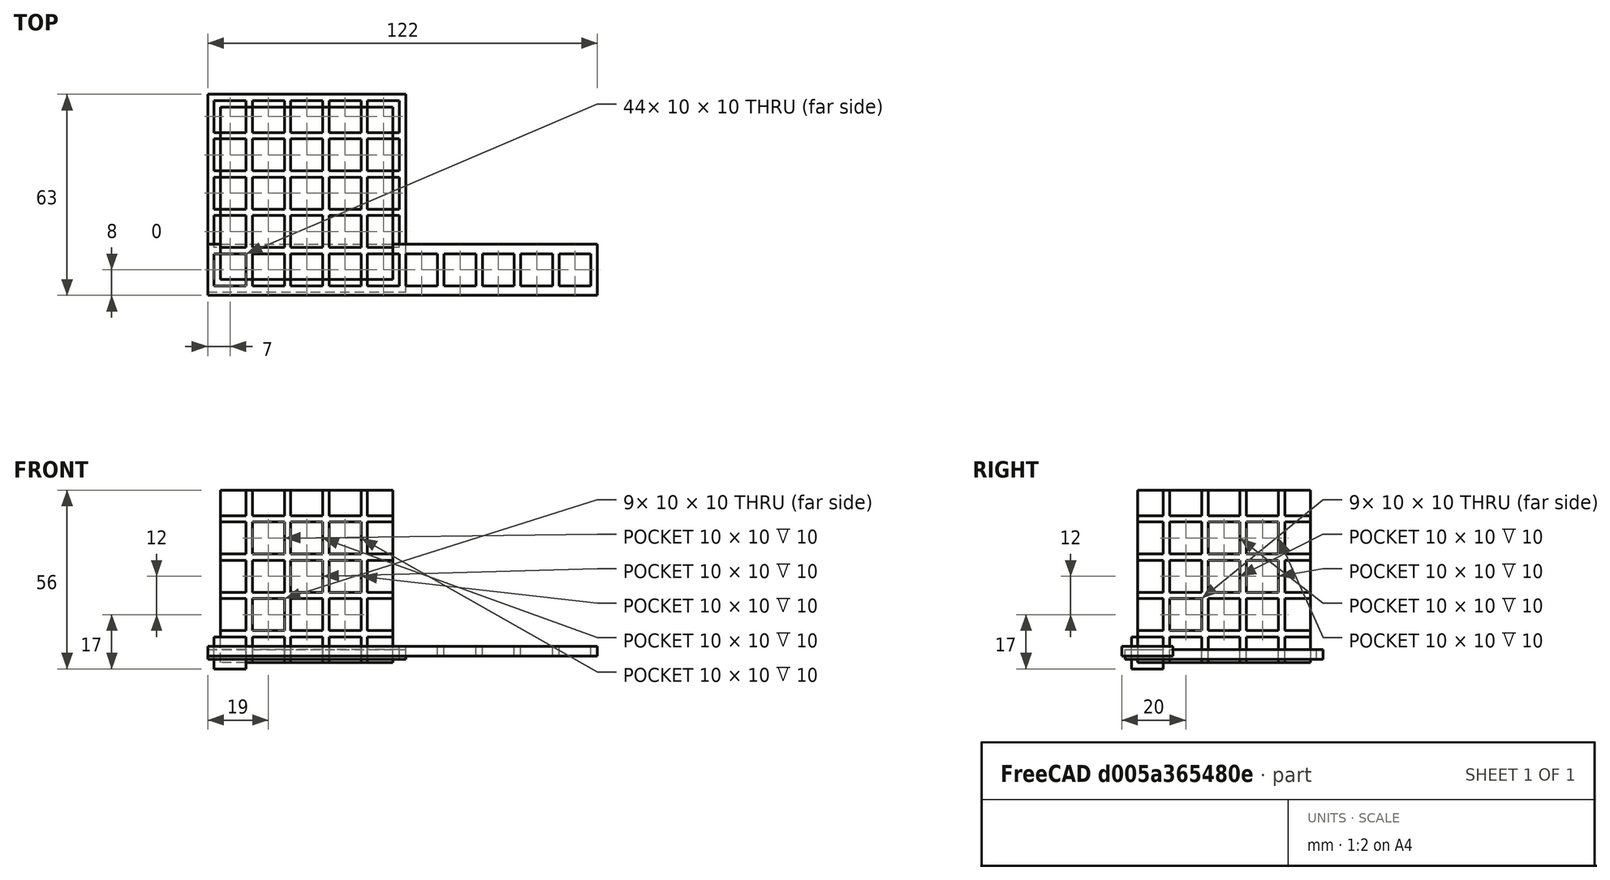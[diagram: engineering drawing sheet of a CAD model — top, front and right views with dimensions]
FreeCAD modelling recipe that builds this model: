
FCSTD DOCUMENT  (FreeCAD 0.21R33771 (Git))
Label: OJT1_T10P01_arrays
License: All rights reserved
LicenseURL: http://en.wikipedia.org/wiki/All_rights_reserved
objects: Part::Box×6, Part::FeaturePython×3, Part::Cut×3
note: 9 computed .brp shape members not serialized (recipe doc carries the construction recipe); baked Part::Feature solids carry a one-line shape summary decoded from their .brp

FEATURE [Part::Box] Box  label="Cube"
  AttacherType = Attacher::AttachEngine3D
  Height = 10
  Length = 10
  Width = 10
FEATURE [Part::FeaturePython] Array  # Draft array (typed FeaturePython)
  AlwaysSyncPlacement = false
  Angle = 360
  ArrayType = 0
  Axis = (0,0,1)
  Base = -> Box
  Center = (0,0,0)
  Count = 10
  ExpandArray = false
  Fuse = false
  IntervalAxis = (0,0,0)
  IntervalX = (12,0,0)
  IntervalY = (0,0,0)
  IntervalZ = (0,0,100)
  NumberCircles = 3
  NumberPolar = 5
  NumberX = 10
  NumberY = 1
  NumberZ = 1
  PlacementList = 10 placements: arithmetic series from (0,0,0) step (12,0,0) to (108,0,0)
  RadialDistance = 50
  ScaleList = (10) [(1,1,1),(1,1,1),(1,1,1),(1,1,1),(1,1,1),(1,1,1),(1,1,1),(1,1,1),(1,1,1),(1,1,1)]
  Symmetry = 1
  TangentialDistance = 25
FEATURE [Part::Box] Box001  label="Cube001"
  AttacherType = Attacher::AttachEngine3D
  Height = 3
  Length = 122
  Placement = pos=(-2,-3,4) rot=(0,0,1;0rad)
  Width = 16
FEATURE [Part::Cut] Cut  label="repeticio_x"
  Base = -> Box001
  Refine = true
  Tool = -> Array
FEATURE [Part::Box] Box002  label="Cube002"
  AttacherType = Attacher::AttachEngine3D
  Height = 10
  Length = 10
  Width = 10
FEATURE [Part::FeaturePython] Array001  # Draft array (typed FeaturePython)
  AlwaysSyncPlacement = false
  Angle = 360
  ArrayType = 0
  Axis = (0,0,1)
  Base = -> Box002
  Center = (0,0,0)
  Count = 25
  ExpandArray = false
  Fuse = false
  IntervalAxis = (0,0,0)
  IntervalX = (12,0,0)
  IntervalY = (0,12,0)
  IntervalZ = (0,0,0)
  NumberCircles = 3
  NumberPolar = 5
  NumberX = 5
  NumberY = 5
  NumberZ = 1
  PlacementList = 25 placements: [(0,0,0),(0,12,0),(0,24,0),(0,36,0),(0,48,0),(12,0,0),(12,12,0),(12,24,0),(12,36,0),(12,48,0),(24,0,0),(24,12,0),(24,24,0),(24,36,0),(24,48,0),(36,0,0),(36,12,0),(36,24,0),(36,36,0),(36,48,0),(48,0,0),(48,12,0),(48,24,0),(48,36,0),(48,48,0)]
  RadialDistance = 50
  ScaleList = (25) [(1,1,1),(1,1,1),(1,1,1),(1,1,1),(1,1,1),(1,1,1),(1,1,1),(1,1,1),(1,1,1),(1,1,1),(1,1,1),(1,1,1),(1,1,1),(1,1,1),(1,1,1),(1,1,1),(1,1,1),(1,1,1),+7 more]
  Symmetry = 1
  TangentialDistance = 25
FEATURE [Part::Box] Box003  label="Cube003"
  AttacherType = Attacher::AttachEngine3D
  Height = 3
  Length = 62
  Placement = pos=(-2,-2,3) rot=(0,0,1;0rad)
  Width = 62
FEATURE [Part::Cut] Cut001  label="repeticio_xy"
  Base = -> Box003
  Refine = true
  Tool = -> Array001
FEATURE [Part::Box] Box004  label="Cube004"
  AttacherType = Attacher::AttachEngine3D
  Height = 10
  Length = 10
  Width = 10
FEATURE [Part::FeaturePython] Array002  # Draft array (typed FeaturePython)
  AlwaysSyncPlacement = false
  Angle = 360
  ArrayType = 0
  Axis = (0,0,1)
  Base = -> Box004
  Center = (0,0,0)
  Count = 125
  ExpandArray = false
  Fuse = false
  IntervalAxis = (0,0,0)
  IntervalX = (12,0,0)
  IntervalY = (0,12,0)
  IntervalZ = (0,0,12)
  NumberCircles = 3
  NumberPolar = 5
  NumberX = 5
  NumberY = 5
  NumberZ = 5
  PlacementList = 125 placements: [(0,0,0),(0,0,12),(0,0,24),(0,0,36),(0,0,48),(0,12,0),(0,12,12),(0,12,24),(0,12,36),(0,12,48),(0,24,0),(0,24,12),(0,24,24),(0,24,36),(0,24,48),(0,36,0),(0,36,12),(0,36,24),(0,36,36),(0,36,48),(0,48,0),(0,48,12),(0,48,24),(0,48,36),(0,48,48),(12,0,0),(12,0,12),(12,0,24),(12,0,36),(12,0,48),(12,12,0),(12,12,12),(12,12,24),(12,12,36),(12,12,48),(12,24,0),(12,24,12),(12,24,24),(12,24,36),(12,24,48),+85 more]
  RadialDistance = 50
  ScaleList = (125) [(1,1,1),(1,1,1),(1,1,1),(1,1,1),(1,1,1),(1,1,1),(1,1,1),(1,1,1),(1,1,1),(1,1,1),(1,1,1),(1,1,1),(1,1,1),(1,1,1),(1,1,1),(1,1,1),(1,1,1),(1,1,1),+107 more]
  Symmetry = 1
  TangentialDistance = 25
FEATURE [Part::Box] Box005  label="Cube005"
  AttacherType = Attacher::AttachEngine3D
  Height = 54
  Length = 54
  Placement = pos=(2,2,2) rot=(0,0,1;0rad)
  Width = 54
FEATURE [Part::Cut] Cut002  label="repeticio_xyz"
  Base = -> Box005
  Refine = true
  Tool = -> Array002
